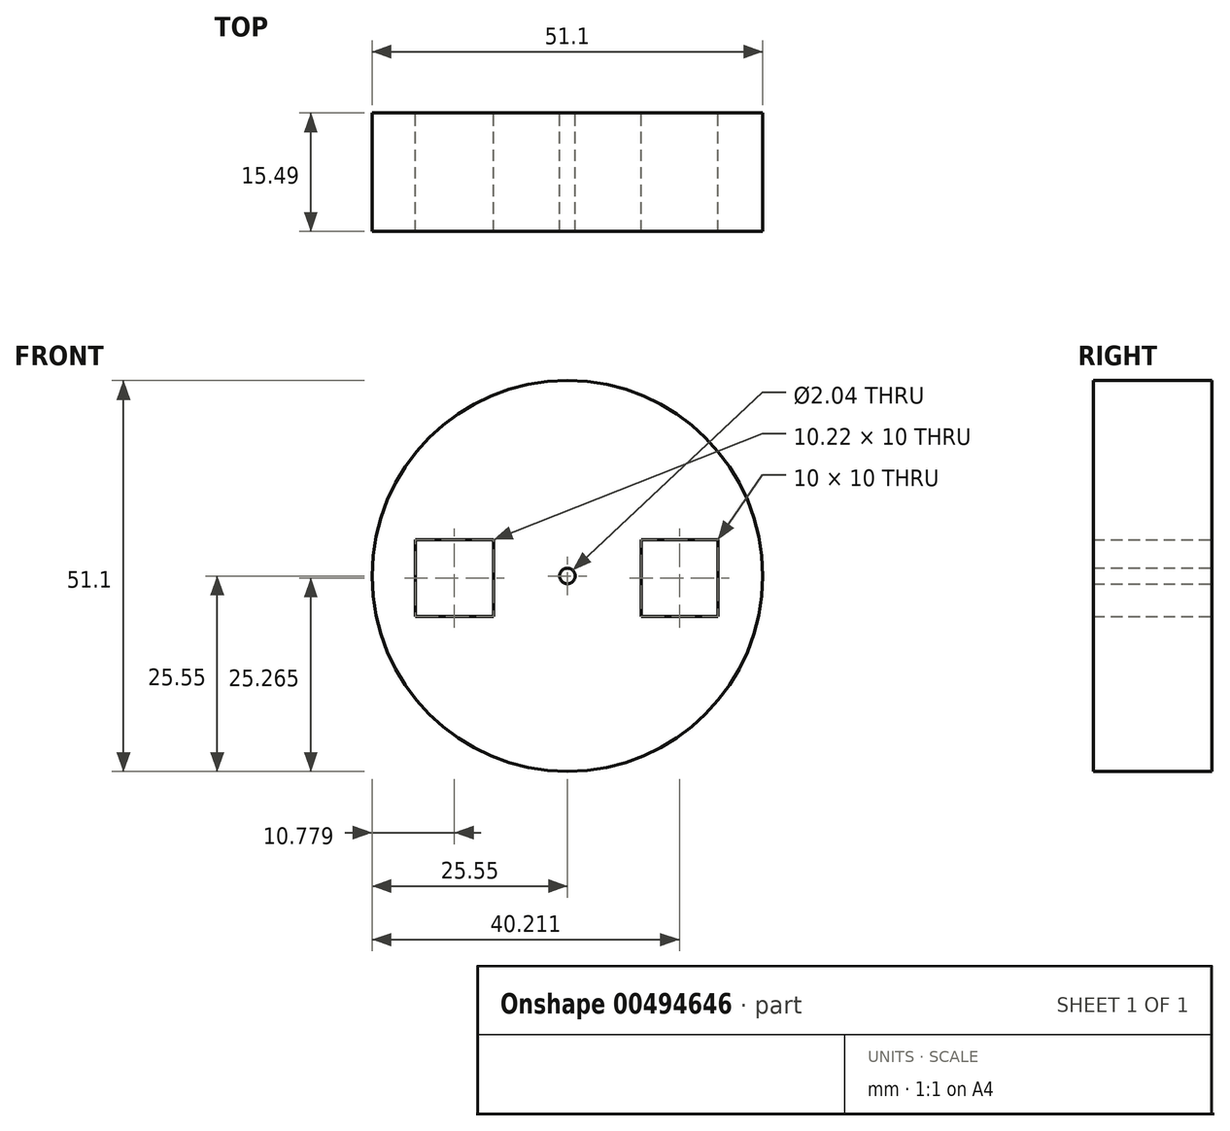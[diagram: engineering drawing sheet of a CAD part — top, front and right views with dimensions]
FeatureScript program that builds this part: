
annotation { "Feature Type Name" : "Feature", "Feature Type Description" : "" }
export const myFeature = defineFeature(function(context is Context, id is Id, definition is map)
    precondition{}
    {
        {
            var Q0;
            Q0=qCreatedBy(makeId("Front.planeOp"),FACE);
            var sketch = newSketch(context, id + "F0", { "sketchPlane" : qUnion([Q0])});
            skCircle(sketch, "E0", {"center": v(0, 0) * mm, "radius": 25.55 * mm});
            skCircle(sketch, "E1", {"center": v(0, 0) * mm, "radius": 1.02 * mm});
            skLineSegment(sketch, "E2.bottom", {"start": v(-19.88, 4.71) * mm, "end": v(-9.66, 4.71) * mm});
            skLineSegment(sketch, "E2.top", {"start": v(-19.88, -5.29) * mm, "end": v(-9.66, -5.29) * mm});
            skLineSegment(sketch, "E2.left", {"start": v(-19.88, 4.71) * mm, "end": v(-19.88, -5.29) * mm});
            skLineSegment(sketch, "E2.right", {"start": v(-9.66, 4.71) * mm, "end": v(-9.66, -5.29) * mm});
            skLineSegment(sketch, "E3.bottom", {"start": v(9.66, -5.29) * mm, "end": v(19.66, -5.29) * mm});
            skLineSegment(sketch, "E3.top", {"start": v(9.66, 4.71) * mm, "end": v(19.66, 4.71) * mm});
            skLineSegment(sketch, "E3.left", {"start": v(9.66, -5.29) * mm, "end": v(9.66, 4.71) * mm});
            skLineSegment(sketch, "E3.right", {"start": v(19.66, -5.29) * mm, "end": v(19.66, 4.71) * mm});
            skSolve(sketch);
        }
        {
            var Q0;
            Q0 = qSketchRegion(id + "F0", true);
            extrude(context, id + "F1", {"entities" : qUnion([Q0]), "depth" : 15.5 * mm});
        }
    });
